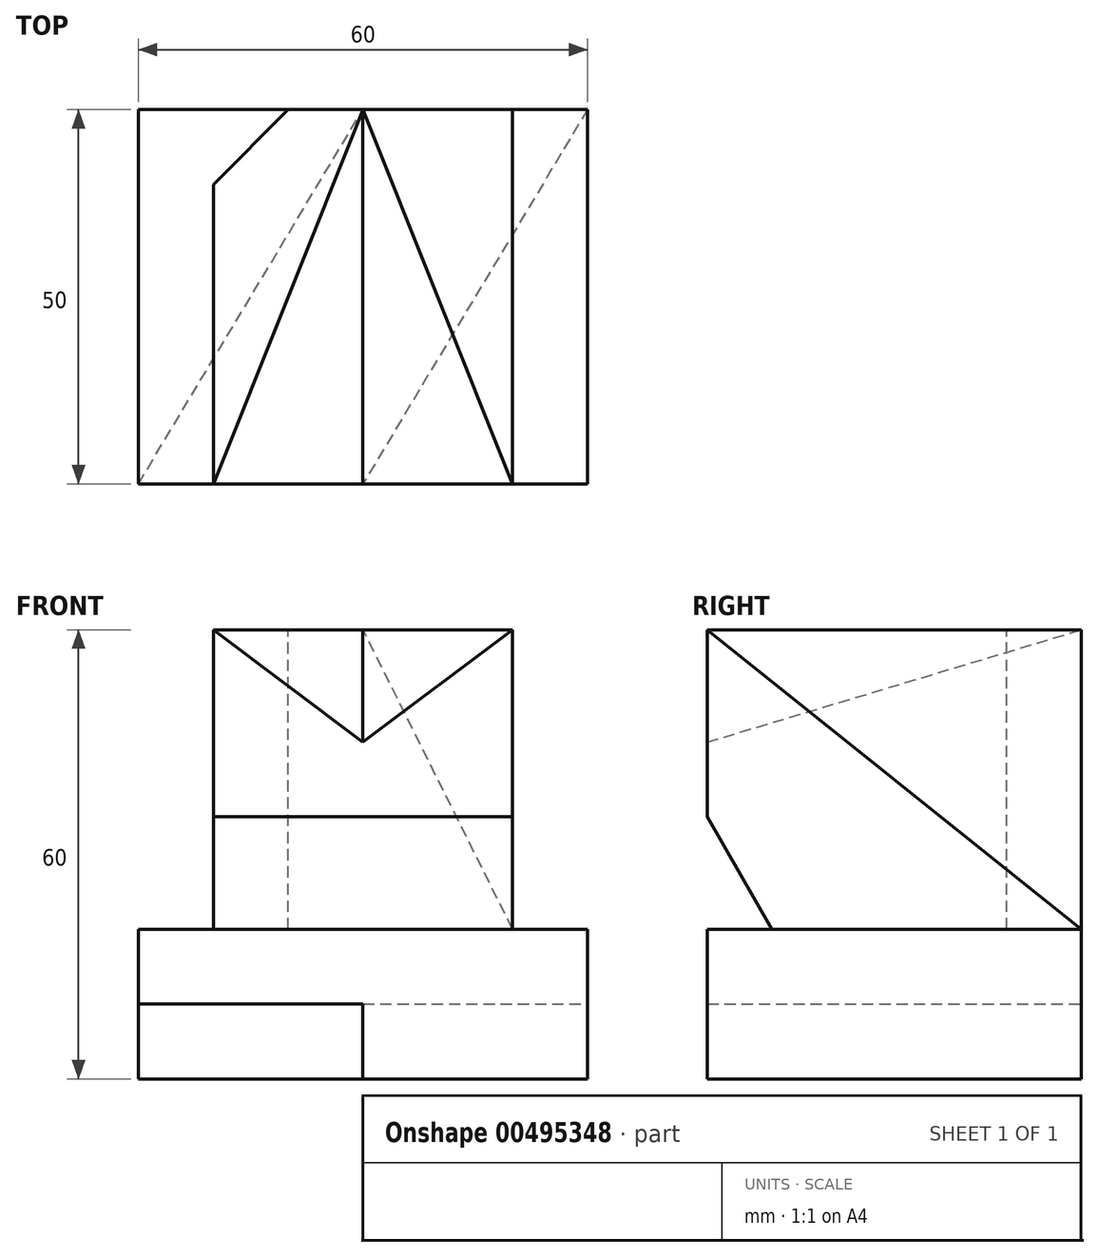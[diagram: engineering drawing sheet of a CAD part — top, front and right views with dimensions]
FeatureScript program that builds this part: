
annotation { "Feature Type Name" : "Feature", "Feature Type Description" : "" }
export const myFeature = defineFeature(function(context is Context, id is Id, definition is map)
    precondition{}
    {
        {
            var Q0;
            Q0=qCreatedBy(makeId("Top.planeOp"),FACE);
            var sketch = newSketch(context, id + "F0", { "sketchPlane" : qUnion([Q0])});
            skLineSegment(sketch, "E0.bottom", {"start": v(0, 0) * mm, "end": v(60, 0) * mm});
            skLineSegment(sketch, "E0.top", {"start": v(0, 50) * mm, "end": v(60, 50) * mm});
            skLineSegment(sketch, "E0.left", {"start": v(0, 0) * mm, "end": v(0, 50) * mm});
            skLineSegment(sketch, "E0.right", {"start": v(60, 0) * mm, "end": v(60, 50) * mm});
            skSolve(sketch);
        }
        {
            var Q0;
            Q0 = qSketchRegion(id + "F0", true);
            extrude(context, id + "F1", {"entities" : qUnion([Q0]), "depth" : 20 * mm});
        }
        {
            var Q0;
            Q0=makeQuery(id+"F1.opExtrude","CAP_FACE",FACE,{"disambiguationData":[OSD([sQuery(id+"F0.wireOp",EDGE,"E0.bottom"),sQuery(id+"F0.wireOp",EDGE,"E0.top"),sQuery(id+"F0.wireOp",EDGE,"E0.left"),sQuery(id+"F0.wireOp",EDGE,"E0.right")])],"isStart":true});
            var sketch = newSketch(context, id + "F2", { "sketchPlane" : qUnion([Q0])});
            skLineSegment(sketch, "E1", {"start": v(0, 0) * mm, "end": v(30, -50) * mm});
            skLineSegment(sketch, "E2", {"start": v(30, -50) * mm, "end": v(60, -50) * mm});
            skLineSegment(sketch, "E3", {"start": v(60, -50) * mm, "end": v(30, 0) * mm});
            skLineSegment(sketch, "E4", {"start": v(30, 0) * mm, "end": v(0, 0) * mm});
            skSolve(sketch);
        }
        {
            var Q0;
            Q0 = qSketchRegion(id + "F2", true);
            extrude(context, id + "F3", {"entities" : qUnion([Q0]), "operationType" : NewBodyOperationType.REMOVE, "oppositeDirection" : true, "depth" : 10 * mm});
        }
        {
            var Q0;
            Q0=makeQuery(id+"F1.opExtrude","CAP_FACE",FACE,{"disambiguationData":[OSD([sQuery(id+"F0.wireOp",EDGE,"E0.bottom"),sQuery(id+"F0.wireOp",EDGE,"E0.top"),sQuery(id+"F0.wireOp",EDGE,"E0.left"),sQuery(id+"F0.wireOp",EDGE,"E0.right")])],"isStart":false});
            var sketch = newSketch(context, id + "F4", { "sketchPlane" : qUnion([Q0])});
            skLineSegment(sketch, "E5.bottom", {"start": v(10, 50) * mm, "end": v(50, 50) * mm});
            skLineSegment(sketch, "E5.top", {"start": v(10, 0) * mm, "end": v(50, 0) * mm});
            skLineSegment(sketch, "E5.left", {"start": v(10, 50) * mm, "end": v(10, 0) * mm});
            skLineSegment(sketch, "E5.right", {"start": v(50, 50) * mm, "end": v(50, 0) * mm});
            skSolve(sketch);
        }
        {
            var Q0;
            Q0 = qSketchRegion(id + "F4", true);
            extrude(context, id + "F5", {"entities" : qUnion([Q0]), "operationType" : NewBodyOperationType.ADD, "depth" : 40 * mm});
        }
        {
            var Q0;
            Q0=makeQuery(id+"F5.opExtrude","SWEPT_FACE",FACE,{"disambiguationData":[OSD([sQuery(id+"F4.wireOp",EDGE,"E5.right")])]});
            var sketch = newSketch(context, id + "F6", { "sketchPlane" : qUnion([Q0])});
            skLineSegment(sketch, "E6", {"start": v(0, 35) * mm, "end": v(8.66, 20) * mm});
            skLineSegment(sketch, "E7", {"start": v(8.66, 20) * mm, "end": v(0, 20) * mm});
            skLineSegment(sketch, "E8", {"start": v(0, 20) * mm, "end": v(0, 35) * mm});
            skSolve(sketch);
        }
        {
            var Q0;
            Q0 = qSketchRegion(id + "F6", true);
            extrude(context, id + "F7", {"entities" : qUnion([Q0]), "operationType" : NewBodyOperationType.REMOVE, "endBound" : BoundingType.UP_TO_NEXT, "oppositeDirection" : true, "depth" : 25 * mm});
        }
        {
            var Q0;
            {var subQ0=sQuery(id+"F4.wireOp",EDGE,"E5.left");var subQ1=sQuery(id+"F4.wireOp",EDGE,"E5.top");var subQ2=sQuery(id+"F4.wireOp",EDGE,"E5.bottom");var subQ3=makeQuery(id+"F5.opExtrude","CAP_FACE",FACE,{"disambiguationData":[OSD([subQ2,subQ1,subQ0,sQuery(id+"F4.wireOp",EDGE,"E5.right")])],"isStart":false});Q0=makeQuery(id+"Fc8OQA63F5NvDiQ_1.boolean.opBoolean","SPLIT",FACE,{"disambiguationData":[TD([makeQuery(id+"F1.opExtrude","SWEPT_FACE",FACE,{"disambiguationData":[OSD([sQuery(id+"F0.wireOp",EDGE,"E0.bottom")])]})])],"derivedFrom":subQ3});}
            var sketch = newSketch(context, id + "F8", { "sketchPlane" : qUnion([Q0])});
            skLineSegment(sketch, "E9", {"start": v(10, 50) * mm, "end": v(20, 50) * mm});
            skLineSegment(sketch, "E10", {"start": v(20, 50) * mm, "end": v(10, 40) * mm});
            skLineSegment(sketch, "E11", {"start": v(10, 40) * mm, "end": v(10, 50) * mm});
            skSolve(sketch);
        }
        {
            var Q0;
            Q0 = qSketchRegion(id + "F8", true);
            extrude(context, id + "F9", {"entities" : qUnion([Q0]), "operationType" : NewBodyOperationType.REMOVE, "oppositeDirection" : true, "depth" : 40 * mm});
        }
        {
            var Q0;
            Q0=makeQuery(id+"F5.opExtrude","SWEPT_FACE",FACE,{"disambiguationData":[OSD([sQuery(id+"F4.wireOp",EDGE,"E5.right")])]});
            cPlane(context, id + "F10", {"entities" : qUnion([Q0]), "cplaneType" : CPlaneType.OFFSET, "offset" : 20 * mm, "oppositeDirection" : true, "width" : 150 * mm, "height" : 150 * mm});
        }
        {
            var Q0;
            {var subQ1=sQuery(id+"F4.wireOp",EDGE,"E5.left");var subQ2=sQuery(id+"F4.wireOp",EDGE,"E5.top");Q0=makeQuery(id+"F7.boolean.opBoolean","SPLIT",FACE,{"disambiguationData":[TD([makeQuery(id+"F5.opExtrude","SWEPT_FACE",FACE,{"disambiguationData":[OSD([subQ1])]})])],"derivedFrom":makeQuery(id+"F5.boolean.opBoolean","MERGE",FACE,{"derivedFrom":[makeQuery(id+"F1.opExtrude","SWEPT_FACE",FACE,{"disambiguationData":[OSD([sQuery(id+"F0.wireOp",EDGE,"E0.bottom")])]}),makeQuery(id+"F5.opExtrude","SWEPT_FACE",FACE,{"disambiguationData":[OSD([subQ2])]})]})});}
            var sketch = newSketch(context, id + "F11", { "sketchPlane" : qUnion([Q0])});
            skLineSegment(sketch, "E12", {"start": v(10, 60) * mm, "end": v(50, 60) * mm});
            skLineSegment(sketch, "E13", {"start": v(50, 60) * mm, "end": v(30, 45) * mm});
            skLineSegment(sketch, "E14", {"start": v(10, 60) * mm, "end": v(30, 45) * mm});
            skSolve(sketch);
        }
        {
            var Q0;
            Q0=qCreatedBy(id+"F10.planeOp",FACE);
            var sketch = newSketch(context, id + "F12", { "sketchPlane" : qUnion([Q0])});
            skLineSegment(sketch, "E15", {"start": v(49.88, 59.86) * mm, "end": v(0, 44.9) * mm});
            skSolve(sketch);
        }
        {
            var Q0;
            Q0=makeQuery(id+"F11.imprint","IMPRINT",FACE,{"disambiguationData":[TD([[makeQuery(id+"F11.imprint","IMPRINT",EDGE,{"derivedFrom":sQuery(id+"F11.wireOp",EDGE,"E12")}),-1.0]])]});
            var Q1;
            Q1=sQuery(id+"F12.wireOp",EDGE,"E15");
            sweep(context, id + "F13", {"operationType" : NewBodyOperationType.REMOVE, "profiles" : qUnion([Q0]), "path" : qUnion([Q1])});
        }
        {
            var Q0;
            {var subQ0=sQuery(id+"F4.wireOp",EDGE,"E5.right");var subQ1=sQuery(id+"F4.wireOp",EDGE,"E5.top");var subQ2=sQuery(id+"F0.wireOp",EDGE,"E0.bottom");Q0=makeQuery(id+"F13.boolean.opBoolean","MERGE",VERTEX,{"derivedFrom":[makeQuery(id+"F5.opExtrude","CAP_VERTEX",VERTEX,{"disambiguationData":[OSD([subQ2,subQ1,subQ0])],"isStart":false}),makeQuery(id+"F13.opSweep","CAP_VERTEX",VERTEX,{"disambiguationData":[OSD([subQ2,subQ1,subQ0,sQuery(id+"F11.wireOp",EDGE,"E12"),sQuery(id+"F11.wireOp",EDGE,"E13"),sQuery(id+"F12.wireOp",EDGE,"E15")])],"isStart":true})]});}
            var Q1;
            {var subQ0=sQuery(id+"F11.wireOp",EDGE,"E13");Q1=makeQuery(id+"F13.boolean.opBoolean","INTERSECT",VERTEX,{"derivedFrom":[makeQuery(id+"F5.opExtrude","CAP_FACE",FACE,{"disambiguationData":[OSD([sQuery(id+"F4.wireOp",EDGE,"E5.bottom"),sQuery(id+"F4.wireOp",EDGE,"E5.top"),sQuery(id+"F4.wireOp",EDGE,"E5.left"),sQuery(id+"F4.wireOp",EDGE,"E5.right")])],"isStart":false}),makeQuery(id+"F13.opSweep","CAP_FACE",FACE,{"disambiguationData":[OSD([sQuery(id+"F11.wireOp",EDGE,"E12"),subQ0,sQuery(id+"F11.wireOp",EDGE,"E14"),sQuery(id+"F12.wireOp",VERTEX,"E15.start")])],"isStart":false}),makeQuery(id+"F13.opSweep","SWEPT_FACE",FACE,{"disambiguationData":[OSD([subQ0,sQuery(id+"F12.wireOp",EDGE,"E15")])]})]});}
            var Q2;
            Q2=makeQuery(id+"F5.opExtrude","CAP_VERTEX",VERTEX,{"disambiguationData":[OSD([sQuery(id+"F0.wireOp",EDGE,"E0.top"),sQuery(id+"F4.wireOp",EDGE,"E5.bottom"),sQuery(id+"F4.wireOp",EDGE,"E5.right")])],"isStart":true});
            cPlane(context, id + "F14", {"entities" : qUnion([Q0, Q1, Q2]), "cplaneType" : CPlaneType.THREE_POINT, "offset" : 25 * mm, "width" : 150 * mm, "height" : 150 * mm});
        }
        {
            var Q0;
            Q0=makeQuery(id+"F5.opExtrude","SWEPT_FACE",FACE,{"disambiguationData":[OSD([sQuery(id+"F4.wireOp",EDGE,"E5.right")])]});
            var sketch = newSketch(context, id + "F15", { "sketchPlane" : qUnion([Q0])});
            skLineSegment(sketch, "E16", {"start": v(0, 60) * mm, "end": v(50, 60) * mm});
            skLineSegment(sketch, "E17", {"start": v(50, 60) * mm, "end": v(50, 20) * mm});
            skLineSegment(sketch, "E18", {"start": v(50, 20) * mm, "end": v(0, 60) * mm});
            skSolve(sketch);
        }
        {
            var Q0;
            Q0 = qSketchRegion(id + "F15", true);
            var Q1;
            Q1=qCreatedBy(id+"F14.planeOp",FACE);
            extrude(context, id + "F16", {"entities" : qUnion([Q0]), "operationType" : NewBodyOperationType.REMOVE, "endBound" : BoundingType.UP_TO_SURFACE, "oppositeDirection" : true, "endBoundEntityFace" : qUnion([Q1]), "depth" : 25 * mm});
        }
    });
